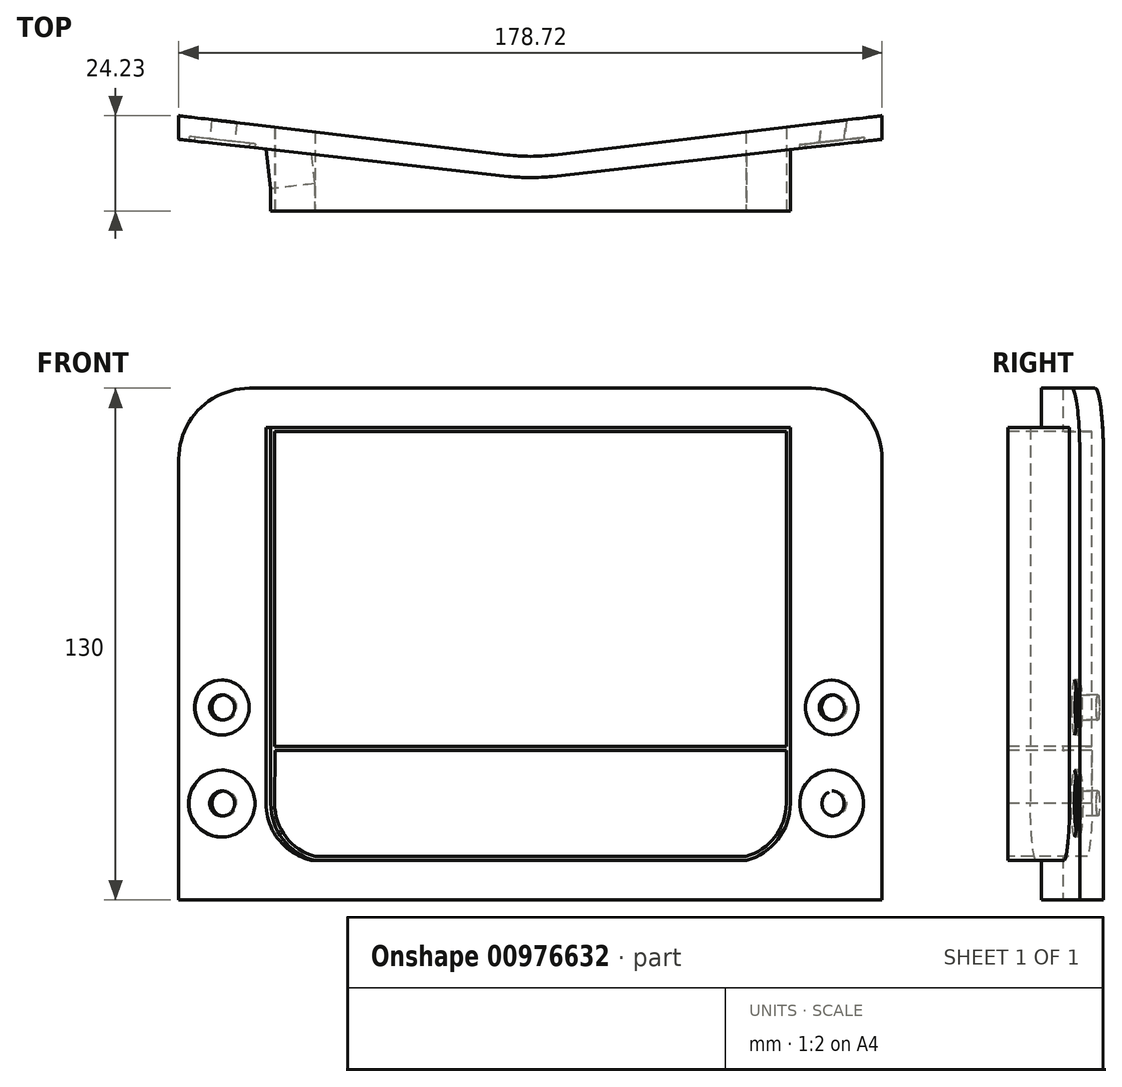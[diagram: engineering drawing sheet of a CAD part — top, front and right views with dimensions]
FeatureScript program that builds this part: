
annotation { "Feature Type Name" : "Feature", "Feature Type Description" : "" }
export const myFeature = defineFeature(function(context is Context, id is Id, definition is map)
    precondition{}
    {
        {
            var Q0;
            Q0=qCreatedBy(makeId("Top.planeOp"),FACE);
            var sketch = newSketch(context, id + "F0", { "sketchPlane" : qUnion([Q0])});
            skLineSegment(sketch, "E0.MirrorCS", {"start": v(461.41, 31.7) * mm, "end": v(461.41, 21.7) * mm});
            skLineSegment(sketch, "E1", {"start": v(0.07, -1.47) * mm, "end": v(-89.36, 9.23) * mm});
            skLineSegment(sketch, "E2", {"start": v(-89.36, 9.23) * mm, "end": v(-89.36, 3.23) * mm});
            skLineSegment(sketch, "E3", {"start": v(-89.36, 3.23) * mm, "end": v(0.07, -6.82) * mm});
            skLineSegment(sketch, "E4.MirrorCS", {"start": v(-0.07, -1.47) * mm, "end": v(89.36, 9.23) * mm});
            skLineSegment(sketch, "E5.MirrorCS", {"start": v(89.36, 3.23) * mm, "end": v(-0.07, -6.82) * mm});
            skLineSegment(sketch, "E6.MirrorCS", {"start": v(89.36, 9.23) * mm, "end": v(89.36, 3.23) * mm});
            skLineSegment(sketch, "E7", {"start": v(-89.36, 9.23) * mm, "end": v(-73.6, 9.23) * mm});
            skSolve(sketch);
        }
        {
            var Q0;
            {var subQ5=sQuery(id+"F0.wireOp",EDGE,"E2");Q0=makeQuery(id+"F0.imprint","IMPRINT",FACE,{"disambiguationData":[TD([[makeQuery(id+"F0.imprint","IMPRINT",EDGE,{"derivedFrom":subQ5}),1.0]])]});}
            extrude(context, id + "F1", {"entities" : qUnion([Q0]), "depth" : 130 * mm, "offsetDistance" : 25 * mm});
        }
        {
            var Q0;
            Q0=makeQuery(id+"F1.opExtrude","SWEPT_EDGE",EDGE,{"disambiguationData":[OSD([sQuery(id+"F0.wireOp",EDGE,"5wA4m7SY-sXlH-00Vl-457M-GXLiX4XNcUin"),sQuery(id+"F0.wireOp",EDGE,"0344254d-ade3-4457-9dcc-b128e93b546e0.MirrorCS")])]});
            var Q1;
            Q1=makeQuery(id+"F1.opExtrude","SWEPT_EDGE",EDGE,{"disambiguationData":[OSD([sQuery(id+"F0.wireOp",EDGE,"E3"),sQuery(id+"F0.wireOp",EDGE,"E5.MirrorCS")])]});
            var Q2;
            Q2=makeQuery(id+"F1.opExtrude","SWEPT_EDGE",EDGE,{"disambiguationData":[OSD([sQuery(id+"F0.wireOp",EDGE,"E1"),sQuery(id+"F0.wireOp",EDGE,"E4.MirrorCS")])]});
            fillet(context, id + "F2", {"entities" : qUnion([Q0, Q1, Q2]), "radius" : 50 * mm, "tangentPropagation" : true, "allowEdgeOverflow" : false});
        }
        {
            var Q0;
            Q0=makeQuery(id+"F1.opExtrude","CAP_EDGE",EDGE,{"disambiguationData":[OSD([sQuery(id+"F0.wireOp",EDGE,"E2")])],"isStart":false});
            var Q1;
            Q1=makeQuery(id+"F1.opExtrude","CAP_EDGE",EDGE,{"disambiguationData":[OSD([sQuery(id+"F0.wireOp",EDGE,"E6.MirrorCS")])],"isStart":false});
            fillet(context, id + "F3", {"entities" : qUnion([Q0, Q1]), "radius" : 18 * mm, "tangentPropagation" : true, "allowEdgeOverflow" : false});
        }
        {
            var Q0;
            Q0=qCreatedBy(makeId("Front.planeOp"),FACE);
            var sketch = newSketch(context, id + "F4", { "sketchPlane" : qUnion([Q0])});
            skLineSegment(sketch, "E8.top", {"start": v(66, 120) * mm, "end": v(-66, 120) * mm});
            skPoint(sketch, "E8.middle", {"position": v(0, 65) * mm});
            skArc(sketch, "E9", {"start": v(-66, 24.47) * mm, "mid": v(-62.88, 15.34) * mm, "end": v(-54.85, 10) * mm});
            skLineSegment(sketch, "E10", {"start": v(-66, 120) * mm, "end": v(-66, 24.47) * mm});
            skArc(sketch, "E11.MirrorCS", {"start": v(66, 24.47) * mm, "mid": v(62.88, 15.34) * mm, "end": v(54.85, 10) * mm});
            skLineSegment(sketch, "E12", {"start": v(66, 120) * mm, "end": v(66, 24.47) * mm});
            skPoint(sketch, "E13.MirrorP", {"position": v(-24.2, 94.09) * mm});
            skLineSegment(sketch, "E14", {"start": v(-62.02, 38) * mm, "end": v(62.02, 38) * mm});
            skLineSegment(sketch, "E15", {"start": v(54.85, 10) * mm, "end": v(-54.85, 10) * mm});
            skLineSegment(sketch, "E16", {"start": v(-62.02, 38) * mm, "end": v(-66, 38) * mm});
            skLineSegment(sketch, "E17", {"start": v(62.02, 38) * mm, "end": v(66, 38) * mm});
            skSolve(sketch);
        }
        {
            var Q0;
            Q0=qSketchRegion(id+"F4",true);
            var Q1;
            Q1=makeQuery(id+"F1.opExtrude","SWEPT_FACE",FACE,{"disambiguationData":[OSD([sQuery(id+"F0.wireOp",EDGE,"E4.MirrorCS")])]});
            extrude(context, id + "F5", {"entities" : qUnion([Q0]), "operationType" : NewBodyOperationType.ADD, "endBound" : BoundingType.UP_TO_SURFACE, "oppositeDirection" : true, "depth" : 25 * mm, "endBoundEntityFace" : qUnion([Q1]), "offsetDistance" : 25 * mm, "hasSecondDirection" : true, "secondDirectionOppositeDirection" : false, "secondDirectionDepth" : 15 * mm});
        }
        {
            var Q0;
            Q0=makeQuery(id+"F5.opExtrude","CAP_FACE",FACE,{"disambiguationData":[OSD([sQuery(id+"F4.wireOp",EDGE,"E8.top"),sQuery(id+"F4.wireOp",EDGE,"E9"),sQuery(id+"F4.wireOp",EDGE,"E10"),sQuery(id+"F4.wireOp",EDGE,"E11.MirrorCS"),sQuery(id+"F4.wireOp",EDGE,"E12"),sQuery(id+"F4.wireOp",EDGE,"E15")])],"isStart":false});
            var sketch = newSketch(context, id + "F6", { "sketchPlane" : qUnion([Q0])});
            skLineSegment(sketch, "E18.0.0", {"start": v(23.4, 120) * mm, "end": v(23.4, 10) * mm});
            skLineSegment(sketch, "E18.0.1", {"start": v(23.4, 10) * mm, "end": v(55.41, 10) * mm});
            skEllipticalArc(sketch, "E18.0.2", {});
            skLineSegment(sketch, "E18.0.3", {"start": v(66.64, 24.47) * mm, "end": v(66.64, 120) * mm});
            skLineSegment(sketch, "E18.0.4", {"start": v(66.64, 120) * mm, "end": v(23.4, 120) * mm});
            const initialGuessF6  = {"E18.0.2": [0.051536799090233155, 0.024498604768274087, 1, 0, 0.015106874318762537, 0.015, 4.971673560998391, 6.281484924342252]};
            skSetInitialGuess(sketch, initialGuessF6);
            skSolve(sketch);
        }
        {
            var Q0;
            Q0 = qSketchRegion(id + "F6", true);
            var Q1;
            Q1=makeQuery(id+"F1.opExtrude","SWEPT_FACE",FACE,{"disambiguationData":[OSD([sQuery(id+"F0.wireOp",EDGE,"E3")])]});
            extrude(context, id + "F7", {"entities" : qUnion([Q0]), "operationType" : NewBodyOperationType.ADD, "endBound" : BoundingType.UP_TO_SURFACE, "depth" : 10 * mm, "endBoundEntityFace" : qUnion([Q1]), "offsetDistance" : 25 * mm});
        }
        {
            var Q0;
            Q0=makeQuery(id+"F5.opExtrude","CAP_FACE",FACE,{"disambiguationData":[OSD([sQuery(id+"F4.wireOp",EDGE,"E8.top"),sQuery(id+"F4.wireOp",EDGE,"E9"),sQuery(id+"F4.wireOp",EDGE,"E10"),sQuery(id+"F4.wireOp",EDGE,"E11.MirrorCS"),sQuery(id+"F4.wireOp",EDGE,"E12"),sQuery(id+"F4.wireOp",EDGE,"E15")])],"isStart":true});
            var sketch = newSketch(context, id + "F8", { "sketchPlane" : qUnion([Q0])});
            skLineSegment(sketch, "E19.0.0", {"start": v(-66, 120) * mm, "end": v(-66, 24.47) * mm});
            skArc(sketch, "E19.0.1", {"start": v(-66, 24.47) * mm, "mid": v(-62.88, 15.34) * mm, "end": v(-54.85, 10) * mm});
            skLineSegment(sketch, "E19.0.2", {"start": v(-54.85, 10) * mm, "end": v(54.85, 10) * mm});
            skArc(sketch, "E19.0.3", {"start": v(54.85, 10) * mm, "mid": v(62.88, 15.34) * mm, "end": v(66, 24.47) * mm});
            skLineSegment(sketch, "E19.0.4", {"start": v(66, 24.47) * mm, "end": v(66, 120) * mm});
            skLineSegment(sketch, "E19.0.5", {"start": v(66, 120) * mm, "end": v(-66, 120) * mm});
            skLineSegment(sketch, "E20.1", {"start": v(65, 119) * mm, "end": v(-65, 119) * mm});
            skLineSegment(sketch, "E21", {"start": v(-66, 24.47) * mm, "end": v(-65, 24.47) * mm});
            skLineSegment(sketch, "E22", {"start": v(-65, 24.47) * mm, "end": v(-65, 119) * mm});
            skArc(sketch, "E23.0", {"start": v(-65, 24.47) * mm, "mid": v(-62.09, 15.95) * mm, "end": v(-54.59, 10.97) * mm});
            skLineSegment(sketch, "E24", {"start": v(-51, 11) * mm, "end": v(-54.59, 10.97) * mm});
            skArc(sketch, "E25.0", {"start": v(54.59, 10.97) * mm, "mid": v(62.09, 15.95) * mm, "end": v(65, 24.47) * mm});
            skLineSegment(sketch, "E26", {"start": v(65, 119) * mm, "end": v(65, 24.47) * mm});
            skLineSegment(sketch, "E27", {"start": v(54.59, 10.97) * mm, "end": v(-51, 11) * mm});
            skLineSegment(sketch, "E28", {"start": v(-51.4, 119) * mm, "end": v(-51.4, 39) * mm, "construction": true});
            skLineSegment(sketch, "E29", {"start": v(-51.4, 39) * mm, "end": v(-65, 39) * mm});
            skLineSegment(sketch, "E30", {"start": v(-51.4, 39) * mm, "end": v(65, 39) * mm});
            skSolve(sketch);
        }
        {
            var Q0;
            {var subQ1=sQuery(id+"F8.wireOp",EDGE,"E20.1");Q0=makeQuery(id+"F8.imprint","IMPRINT",FACE,{"disambiguationData":[TD([[makeQuery(id+"F8.imprint","IMPRINT",EDGE,{"derivedFrom":subQ1}),1.0]])]});}
            extrude(context, id + "F9", {"entities" : qUnion([Q0]), "operationType" : NewBodyOperationType.REMOVE, "oppositeDirection" : true, "depth" : 37 * mm, "offsetDistance" : 25 * mm});
        }
        {
            var Q0;
            Q0=makeQuery(id+"F5.opExtrude","CAP_FACE",FACE,{"disambiguationData":[OSD([sQuery(id+"F4.wireOp",EDGE,"E8.top"),sQuery(id+"F4.wireOp",EDGE,"E9"),sQuery(id+"F4.wireOp",EDGE,"E10"),sQuery(id+"F4.wireOp",EDGE,"E11.MirrorCS"),sQuery(id+"F4.wireOp",EDGE,"E12"),sQuery(id+"F4.wireOp",EDGE,"E15")])],"isStart":true});
            var sketch = newSketch(context, id + "F10", { "sketchPlane" : qUnion([Q0])});
            skLineSegment(sketch, "E31.0.0", {"start": v(-66, 120) * mm, "end": v(-66, 24.47) * mm});
            skArc(sketch, "E31.0.1", {"start": v(-66, 24.47) * mm, "mid": v(-62.88, 15.34) * mm, "end": v(-54.85, 10) * mm});
            skLineSegment(sketch, "E31.0.2", {"start": v(-54.85, 10) * mm, "end": v(54.85, 10) * mm});
            skArc(sketch, "E31.0.3", {"start": v(54.85, 10) * mm, "mid": v(62.88, 15.34) * mm, "end": v(66, 24.47) * mm});
            skLineSegment(sketch, "E31.0.4", {"start": v(66, 24.47) * mm, "end": v(66, 120) * mm});
            skLineSegment(sketch, "E31.0.5", {"start": v(66, 120) * mm, "end": v(-66, 120) * mm});
            skLineSegment(sketch, "E32.0", {"start": v(-51.4, 39) * mm, "end": v(65, 39) * mm});
            skLineSegment(sketch, "E33.0", {"start": v(-51.4, 39) * mm, "end": v(-65, 39) * mm});
            skSolve(sketch);
        }
        {
            var Q0;
            Q0=makeQuery(id+"F10.imprint","IMPRINT",FACE,{"disambiguationData":[TD([[makeQuery(id+"F10.imprint","IMPRINT",EDGE,{"derivedFrom":sQuery(id+"F10.wireOp",EDGE,"E31.0.0")}),1.0]])]});
            var sketch = newSketch(context, id + "F11", { "sketchPlane" : qUnion([Q0])});
            skLineSegment(sketch, "E34", {"start": v(-65.88, 38.9) * mm, "end": v(66, 38.9) * mm});
            skLineSegment(sketch, "E35.0", {"start": v(-54.85, 10) * mm, "end": v(54.85, 10) * mm});
            skArc(sketch, "E36.0", {"start": v(-66, 24.47) * mm, "mid": v(-62.88, 15.34) * mm, "end": v(-54.85, 10) * mm});
            skLineSegment(sketch, "E37", {"start": v(-65.88, 38.9) * mm, "end": v(-66, 24.47) * mm});
            skPoint(sketch, "E38.0", {"position": v(51, 24.5) * mm});
            skArc(sketch, "E39.0.4", {"start": v(54.85, 10) * mm, "mid": v(62.88, 15.34) * mm, "end": v(66, 24.47) * mm});
            skLineSegment(sketch, "E40", {"start": v(66, 38.9) * mm, "end": v(66, 24.47) * mm});
            skLineSegment(sketch, "E41.0", {"start": v(-64.89, 37.9) * mm, "end": v(-65, 24.47) * mm});
            skLineSegment(sketch, "E41.1", {"start": v(65, 37.9) * mm, "end": v(65, 24.47) * mm});
            skArc(sketch, "E41.2", {"start": v(54.71, 11) * mm, "mid": v(62.13, 16) * mm, "end": v(65, 24.47) * mm});
            skLineSegment(sketch, "E41.3", {"start": v(-64.89, 37.9) * mm, "end": v(65, 37.9) * mm});
            skLineSegment(sketch, "E41.4", {"start": v(-54.71, 11) * mm, "end": v(54.71, 11) * mm});
            skArc(sketch, "E41.5", {"start": v(-65, 24.47) * mm, "mid": v(-62.13, 16) * mm, "end": v(-54.71, 11) * mm});
            skLineSegment(sketch, "E42.0", {"start": v(-51.4, 39) * mm, "end": v(65, 39) * mm, "construction": true});
            skSolve(sketch);
        }
        {
            var Q0;
            Q0=makeQuery(id+"F11.imprint","IMPRINT",FACE,{"disambiguationData":[TD([[makeQuery(id+"F11.imprint","IMPRINT",EDGE,{"derivedFrom":sQuery(id+"F11.wireOp",EDGE,"E41.0")}),1.0]])]});
            extrude(context, id + "F12", {"entities" : qUnion([Q0]), "operationType" : NewBodyOperationType.REMOVE, "oppositeDirection" : true, "depth" : 37 * mm, "offsetDistance" : 25 * mm});
        }
        {
            var Q0;
            Q0=makeQuery(id+"F1.opExtrude","SWEPT_FACE",FACE,{"disambiguationData":[OSD([sQuery(id+"F0.wireOp",EDGE,"E3")])]});
            var sketch = newSketch(context, id + "F13", { "sketchPlane" : qUnion([Q0])});
            skCircle(sketch, "E43", {"center": v(-78.17, 48.87) * mm, "radius": 7 * mm});
            skCircle(sketch, "E44", {"center": v(-78.17, 48.87) * mm, "radius": 3.2 * mm});
            skLineSegment(sketch, "E45", {"start": v(-66.87, 48.87) * mm, "end": v(-89.17, 48.87) * mm, "construction": true});
            skLineSegment(sketch, "E46", {"start": v(-89.17, 48.87) * mm, "end": v(-78.17, 48.87) * mm, "construction": true});
            skLineSegment(sketch, "E47", {"start": v(-78.17, 48.87) * mm, "end": v(-78.17, 10.92) * mm, "construction": true});
            skPoint(sketch, "E48.0", {"position": v(-66.87, 24.47) * mm});
            skLineSegment(sketch, "E49", {"start": v(-66.87, 24.47) * mm, "end": v(-78.17, 24.47) * mm, "construction": true});
            skCircle(sketch, "E50", {"center": v(-78.17, 24.47) * mm, "radius": 8.5 * mm});
            skCircle(sketch, "E51", {"center": v(-78.17, 24.47) * mm, "radius": 3.2 * mm});
            skSolve(sketch);
        }
        {
            var Q0;
            Q0=makeQuery(id+"F1.opExtrude","SWEPT_FACE",FACE,{"disambiguationData":[OSD([sQuery(id+"F0.wireOp",EDGE,"E5.MirrorCS")])]});
            var sketch = newSketch(context, id + "F14", { "sketchPlane" : qUnion([Q0])});
            skEllipse(sketch, "E52.0", {"center": v(76.2, 24.47) * mm, "majorRadius": 8.5 * mm, "minorRadius": 8.29 * mm, "majorAxis": v(0, -1)});
            skEllipse(sketch, "E53.0", {"center": v(76.2, 24.47) * mm, "majorRadius": 3.2 * mm, "minorRadius": 3.12 * mm, "majorAxis": v(0, -1)});
            skEllipse(sketch, "E54.0", {"center": v(76.2, 48.87) * mm, "majorRadius": 7 * mm, "minorRadius": 6.83 * mm, "majorAxis": v(0, -1)});
            skCircle(sketch, "E55", {"center": v(76.2, 48.87) * mm, "radius": 3.2 * mm});
            skSolve(sketch);
        }
        {
            var Q0;
            Q0=makeQuery(id+"F13.imprint","IMPRINT",FACE,{"disambiguationData":[TD([[makeQuery(id+"F13.imprint","IMPRINT",EDGE,{"derivedFrom":sQuery(id+"F13.wireOp",EDGE,"E44")}),1.0]])]});
            var Q1;
            Q1=makeQuery(id+"F13.imprint","IMPRINT",FACE,{"disambiguationData":[TD([[makeQuery(id+"F13.imprint","IMPRINT",EDGE,{"derivedFrom":sQuery(id+"F13.wireOp",EDGE,"E51")}),1.0]])]});
            var Q2;
            Q2=makeQuery(id+"F14.imprint","IMPRINT",FACE,{"disambiguationData":[TD([[makeQuery(id+"F14.imprint","IMPRINT",EDGE,{"derivedFrom":sQuery(id+"F14.wireOp",EDGE,"E55")}),1.0]])]});
            var Q3;
            Q3=makeQuery(id+"F14.imprint","IMPRINT",FACE,{"disambiguationData":[TD([[makeQuery(id+"F14.imprint","IMPRINT",EDGE,{"derivedFrom":sQuery(id+"F14.wireOp",EDGE,"E53.0")}),1.0]])]});
            extrude(context, id + "F15", {"entities" : qUnion([Q0, Q1, Q2, Q3]), "operationType" : NewBodyOperationType.REMOVE, "oppositeDirection" : true, "depth" : 25 * mm, "offsetDistance" : 25 * mm});
        }
        {
            var Q0;
            Q0=makeQuery(id+"F13.imprint","IMPRINT",FACE,{"disambiguationData":[TD([[makeQuery(id+"F13.imprint","IMPRINT",EDGE,{"derivedFrom":sQuery(id+"F13.wireOp",EDGE,"E43")}),1.0]])]});
            var Q1;
            Q1=makeQuery(id+"F13.imprint","IMPRINT",FACE,{"disambiguationData":[TD([[makeQuery(id+"F13.imprint","IMPRINT",EDGE,{"derivedFrom":sQuery(id+"F13.wireOp",EDGE,"E50")}),1.0]])]});
            var Q2;
            Q2=makeQuery(id+"F14.imprint","IMPRINT",FACE,{"disambiguationData":[TD([[makeQuery(id+"F14.imprint","IMPRINT",EDGE,{"derivedFrom":sQuery(id+"F14.wireOp",EDGE,"E52.0")}),1.0]])]});
            var Q3;
            Q3=makeQuery(id+"F14.imprint","IMPRINT",FACE,{"disambiguationData":[TD([[makeQuery(id+"F14.imprint","IMPRINT",EDGE,{"derivedFrom":sQuery(id+"F14.wireOp",EDGE,"E54.0")}),1.0]])]});
            extrude(context, id + "F16", {"entities" : qUnion([Q0, Q1, Q2, Q3]), "operationType" : NewBodyOperationType.REMOVE, "oppositeDirection" : true, "depth" : 1 * mm, "offsetDistance" : 25 * mm});
        }
    });
